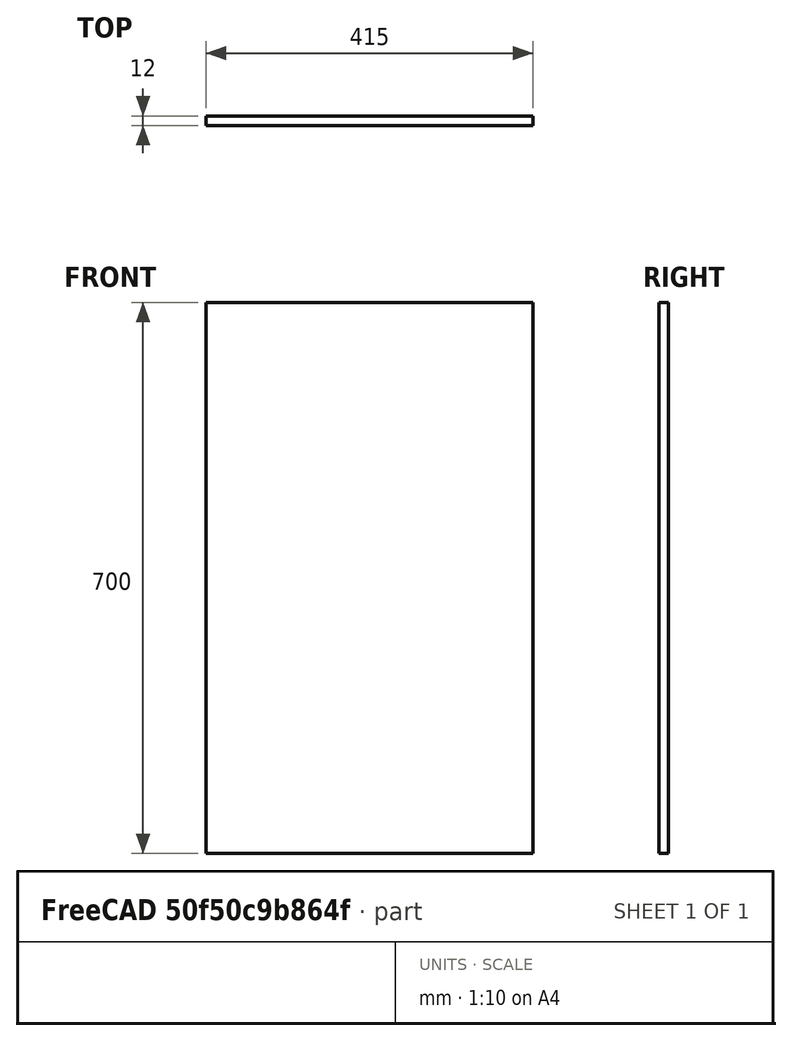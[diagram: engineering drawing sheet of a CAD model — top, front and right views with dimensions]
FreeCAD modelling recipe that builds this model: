
FCSTD DOCUMENT  (FreeCAD 0.20R29603 (Git))
Label: 500_Pedastil_Sides
License: All rights reserved
LicenseURL: http://en.wikipedia.org/wiki/All_rights_reserved
objects: Sketcher::SketchObject×1, PartDesign::Pad×1, PartDesign::Body×1
note: 4 computed .brp shape members not serialized (recipe doc carries the construction recipe); baked Part::Feature solids carry a one-line shape summary decoded from their .brp

FEATURE [Sketcher::SketchObject] Sketch
  FullyConstrained = true
  MapMode = 5
  Placement = pos=(0,0,0) rot=(1,0,0;1.5708rad)
  Support = -> [XZ_Plane]
  sketch-geometry (4):
    g0: LineSegment StartX=0 StartY=0 StartZ=0 EndX=415 EndY=0 EndZ=0
    g1: LineSegment StartX=415 StartY=0 StartZ=0 EndX=415 EndY=700 EndZ=0
    g2: LineSegment StartX=415 StartY=700 StartZ=0 EndX=0 EndY=700 EndZ=0
    g3: LineSegment StartX=0 StartY=700 StartZ=0 EndX=0 EndY=0 EndZ=0
  constraints (11):
    c: Coincident(g0,g1)
    c: Coincident(g1,g2)
    c: Coincident(g2,g3)
    c: Coincident(g3,g0)
    c: Horizontal(g0)
    c: Horizontal(g2)
    c: Vertical(g1)
    c: Vertical(g3)
    c: Coincident(g0,g-1)
    c: DistanceX(g2,g2) = 415
    c: DistanceY(g1,g1) = 700
FEATURE [PartDesign::Pad] Pad
  Direction = (0,-1,-2e-16)
  Length = 12
  Length2 = 100
  Placement = pos=(0,0,0) rot=(1,0,0;1.5708rad)
  Profile = -> Sketch
  Reversed = true
  Type = 0
FEATURE [PartDesign::Body] Body
  Group = -> [Sketch,Pad]
  Origin = -> Origin
  Tip = -> Pad
